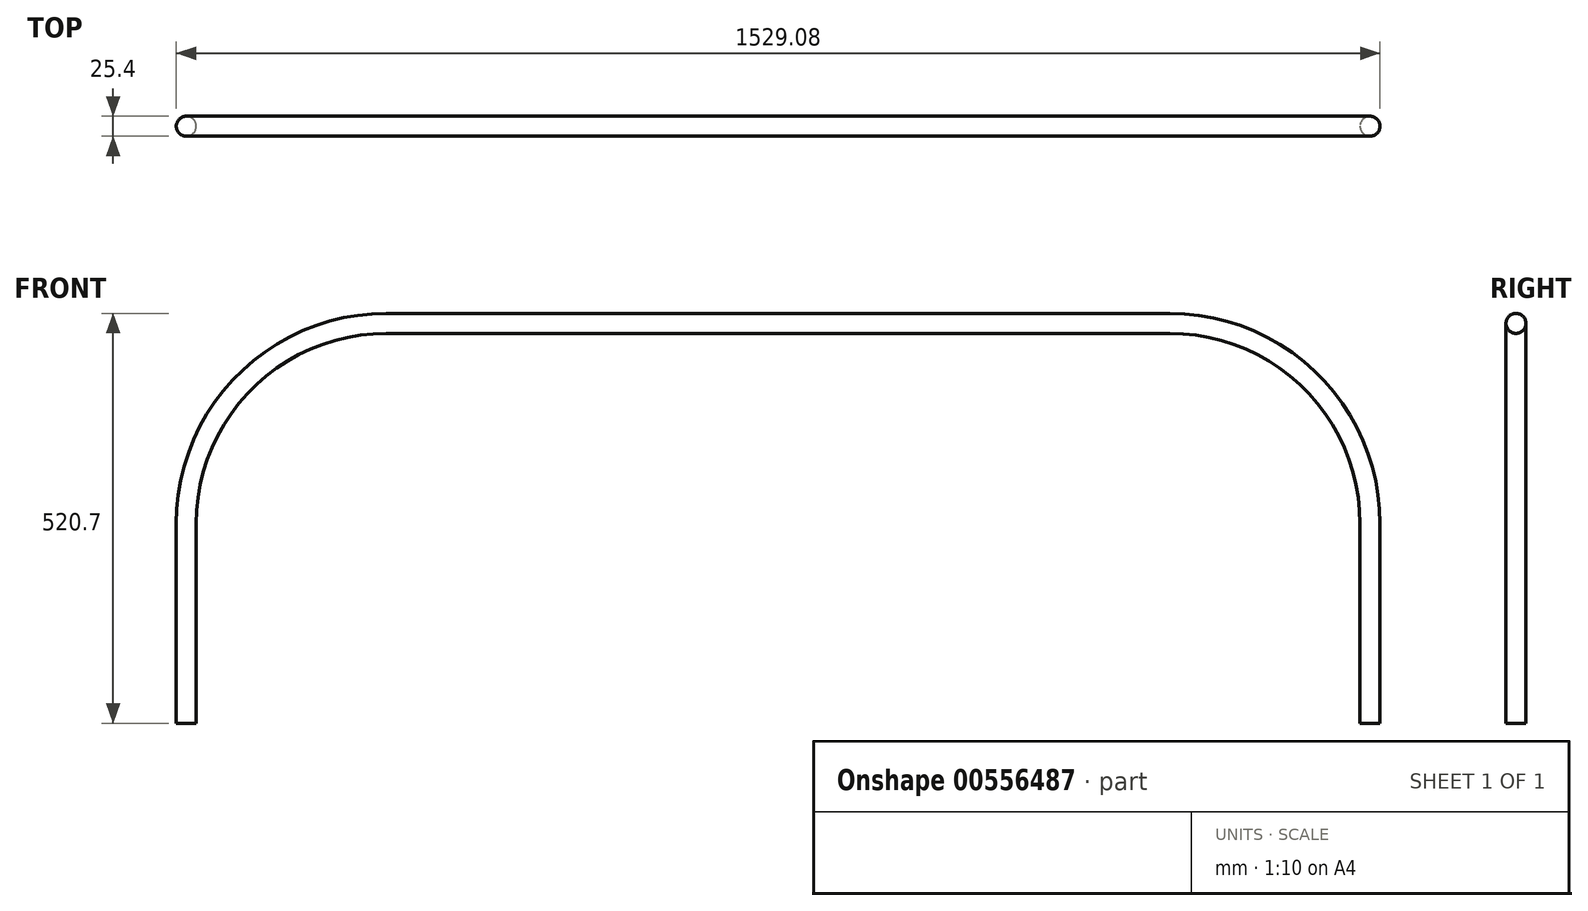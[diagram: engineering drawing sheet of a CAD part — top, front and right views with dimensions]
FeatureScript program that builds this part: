
annotation { "Feature Type Name" : "Feature", "Feature Type Description" : "" }
export const myFeature = defineFeature(function(context is Context, id is Id, definition is map)
    precondition{}
    {
        {
            var Q0;
            Q0=qCreatedBy(makeId("Front.planeOp"),FACE);
            var sketch = newSketch(context, id + "F0", { "sketchPlane" : qUnion([Q0])});
            skLineSegment(sketch, "E0", {"start": v(0, 0) * mm, "end": v(0, 254) * mm});
            skArc(sketch, "E1", {"start": v(0, 254) * mm, "mid": v(74.4, 433.6) * mm, "end": v(254, 508) * mm});
            skLineSegment(sketch, "E2", {"start": v(254, 508) * mm, "end": v(1249.68, 508) * mm});
            skArc(sketch, "E3", {"start": v(1249.68, 508) * mm, "mid": v(1429.29, 433.6) * mm, "end": v(1503.68, 254) * mm});
            skLineSegment(sketch, "E4", {"start": v(1503.68, 254) * mm, "end": v(1503.68, 0) * mm});
            skLineSegment(sketch, "E5", {"start": v(1490.98, 0) * mm, "end": v(1503.68, 0) * mm});
            skSolve(sketch);
        }
        {
            var Q0;
            Q0=qCreatedBy(makeId("Top.planeOp"),FACE);
            var sketch = newSketch(context, id + "F1", { "sketchPlane" : qUnion([Q0])});
            skCircle(sketch, "E6", {"center": v(0, 0) * mm, "radius": 12.7 * mm});
            skSolve(sketch);
        }
        {
            var Q0;
            Q0=makeQuery(id+"F1.imprint","IMPRINT",FACE,{"disambiguationData":[TD([[makeQuery(id+"F1.imprint","IMPRINT",EDGE,{"derivedFrom":sQuery(id+"F1.wireOp",EDGE,"E6")}),1.0]])]});
            var Q1;
            Q1=sQuery(id+"F0.wireOp",EDGE,"E0");
            var Q2;
            Q2=sQuery(id+"F0.wireOp",EDGE,"E1");
            var Q3;
            Q3=sQuery(id+"F0.wireOp",EDGE,"E2");
            var Q4;
            Q4=sQuery(id+"F0.wireOp",EDGE,"E3");
            var Q5;
            Q5=sQuery(id+"F0.wireOp",EDGE,"E4");
            sweep(context, id + "F2", {"profiles" : qUnion([Q0]), "path" : qUnion([Q1, Q2, Q3, Q4, Q5])});
        }
    });
